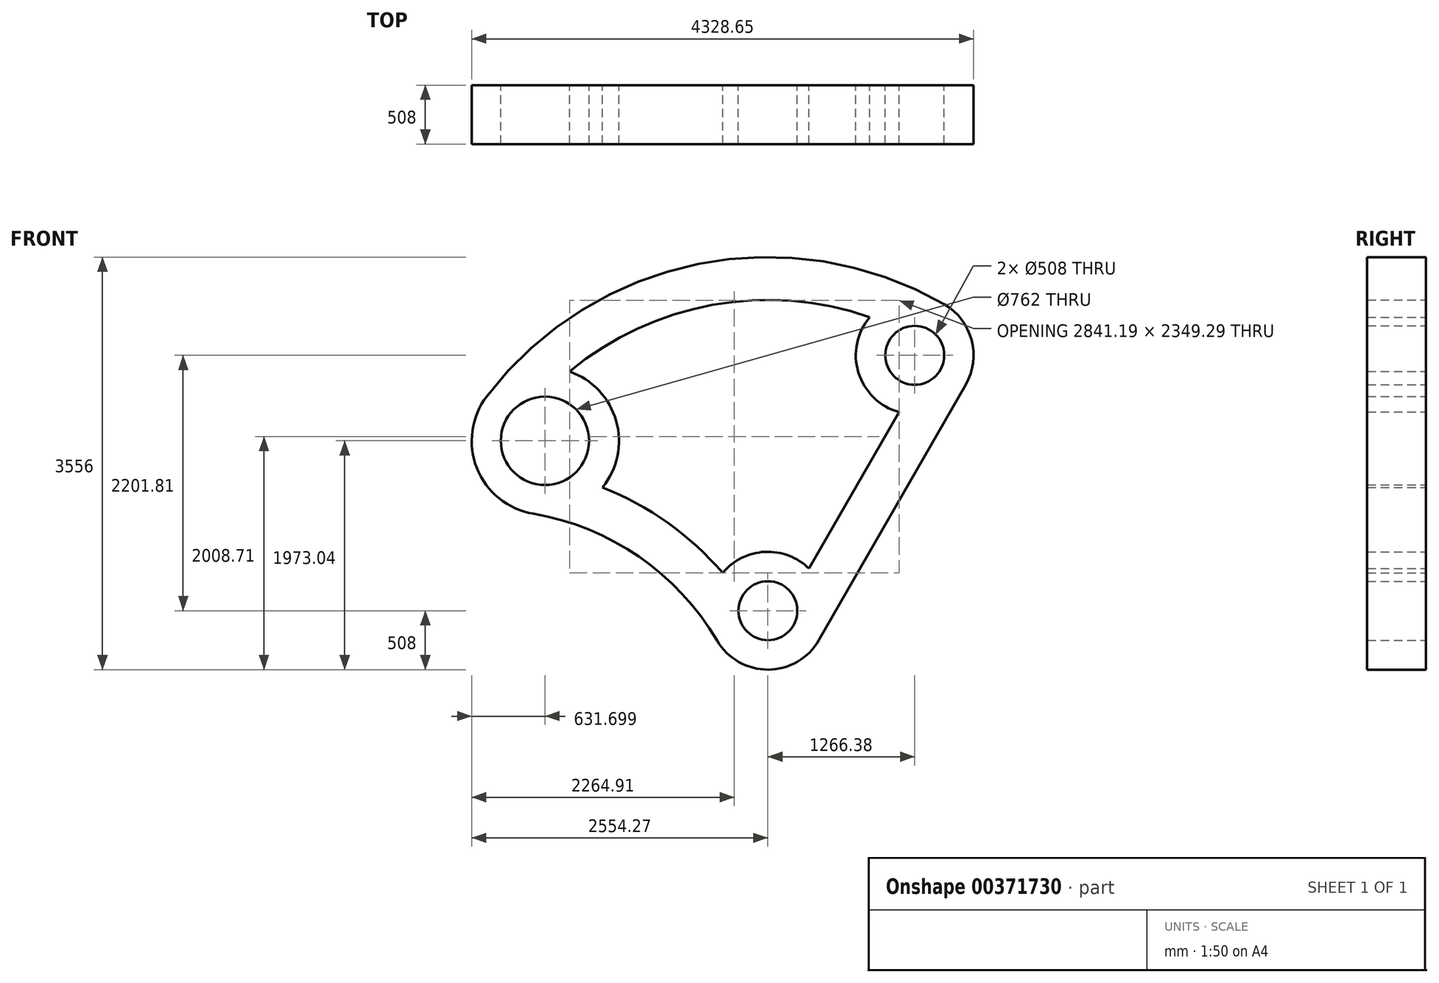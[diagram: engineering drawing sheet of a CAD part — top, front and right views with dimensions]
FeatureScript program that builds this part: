
annotation { "Feature Type Name" : "Feature", "Feature Type Description" : "" }
export const myFeature = defineFeature(function(context is Context, id is Id, definition is map)
    precondition{}
    {
        {
            var Q0;
            Q0=qCreatedBy(makeId("Front.planeOp"),FACE);
            var sketch = newSketch(context, id + "F0", { "sketchPlane" : qUnion([Q0])});
            skArc(sketch, "E0", {"start": v(879.02, 2530.47) * mm, "mid": v(-476.94, 2636) * mm, "end": v(-1709.95, 2062.04) * mm});
            skArc(sketch, "E1", {"start": v(1524, 2639.65) * mm, "mid": v(-599.64, 2988.43) * mm, "end": v(-2424.34, 1847.4) * mm});
            skCircle(sketch, "E2", {"center": v(1266.38, 2201.81) * mm, "radius": 254 * mm});
            skCircle(sketch, "E3", {"center": v(-1922.57, 1465.04) * mm, "radius": 381 * mm});
            skCircle(sketch, "E4", {"center": v(0, 0) * mm, "radius": 254 * mm});
            skArc(sketch, "E5", {"start": v(879.02, 2530.47) * mm, "mid": v(780.92, 2052.19) * mm, "end": v(1131.24, 1712.12) * mm});
            skLineSegment(sketch, "E6", {"start": v(1706.74, 1948.54) * mm, "end": v(440.36, -253.27) * mm});
            skArc(sketch, "E7.trimOffspring", {"start": v(1706.74, 1948.54) * mm, "mid": v(1757.5, 2331.67) * mm, "end": v(1524, 2639.65) * mm});
            skLineSegment(sketch, "E8.trimOffspring", {"start": v(355.32, 363.06) * mm, "end": v(1131.24, 1712.12) * mm});
            skPoint(sketch, "E9.visualSharp", {"position": v(-3.62, 2.1) * mm});
            skArc(sketch, "E10", {"start": v(-437.79, -257.7) * mm, "mid": v(-1110.62, 464.98) * mm, "end": v(-2025.48, 836.47) * mm});
            skArc(sketch, "E11.0", {"start": v(-389.54, 326.07) * mm, "mid": v(-863.33, 756.93) * mm, "end": v(-1426.16, 1062.44) * mm});
            skArc(sketch, "E12", {"start": v(-2424.34, 1847.4) * mm, "mid": v(-2509.95, 1229.47) * mm, "end": v(-2025.48, 836.47) * mm});
            skArc(sketch, "E13.trimOffspring", {"start": v(-1426.16, 1062.44) * mm, "mid": v(-1308.4, 1635.95) * mm, "end": v(-1709.95, 2062.04) * mm});
            skArc(sketch, "E14.trimOffspring", {"start": v(-437.79, -257.7) * mm, "mid": v(2.56, -508) * mm, "end": v(440.36, -253.27) * mm});
            skArc(sketch, "E15.trimOffspring", {"start": v(355.32, 363.06) * mm, "mid": v(-25.2, 507.37) * mm, "end": v(-389.54, 326.07) * mm});
            skSolve(sketch);
        }
        {
            var Q0;
            Q0=makeQuery(id+"F0.imprint","IMPRINT",FACE,{"disambiguationData":[TD([[makeQuery(id+"F0.imprint","IMPRINT",EDGE,{"derivedFrom":sQuery(id+"F0.wireOp",EDGE,"E0")}),-1.0]])]});
            extrude(context, id + "F1", {"entities" : qUnion([Q0]), "depth" : 508 * mm});
        }
    });
